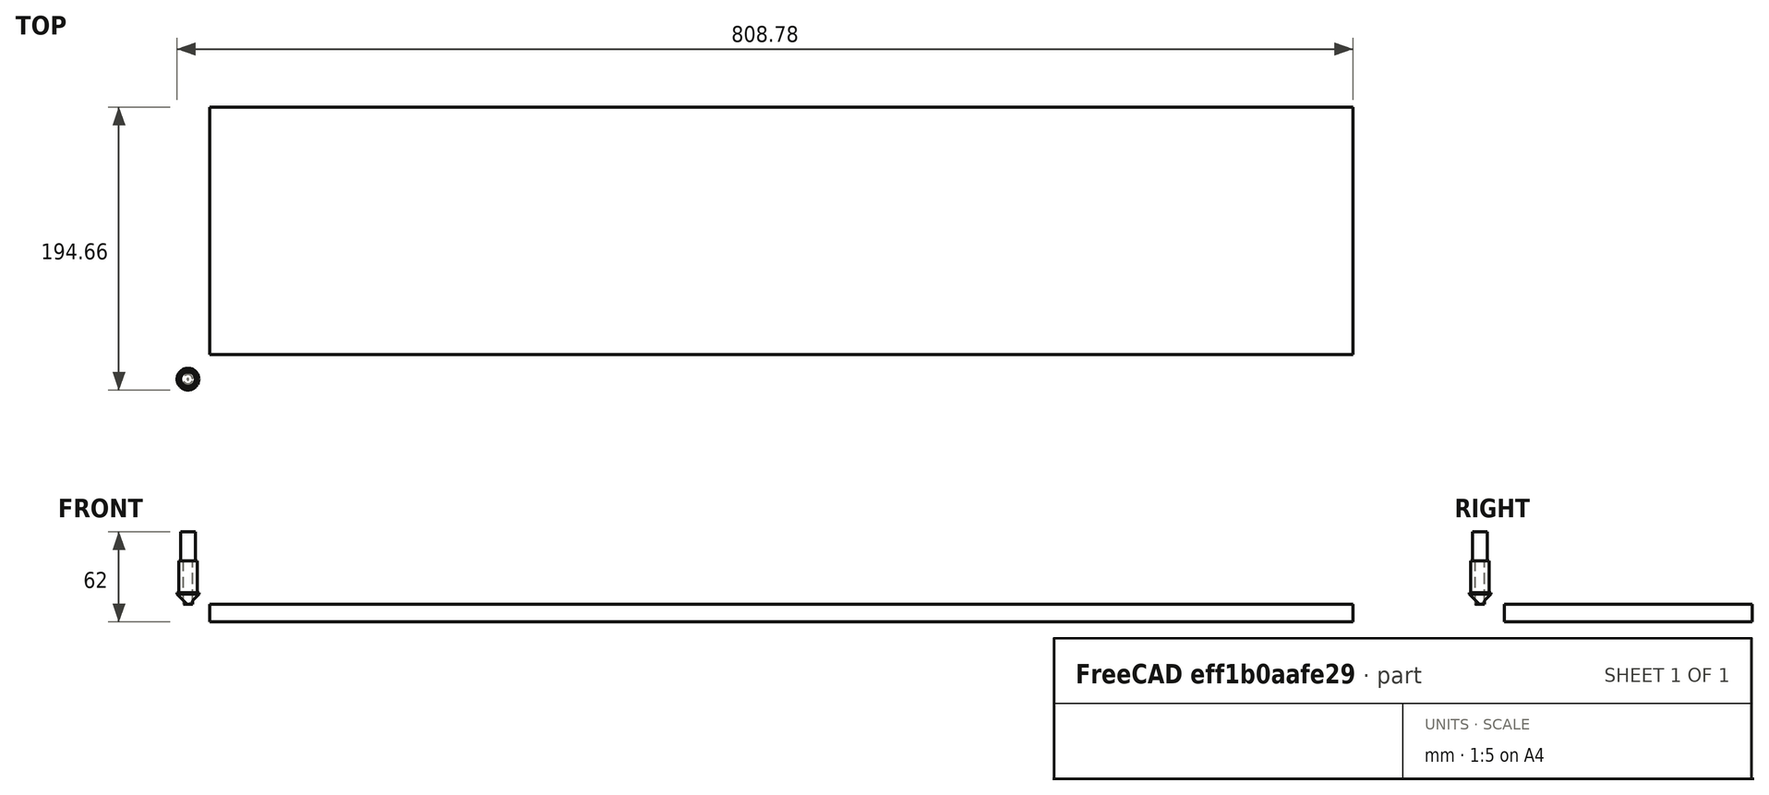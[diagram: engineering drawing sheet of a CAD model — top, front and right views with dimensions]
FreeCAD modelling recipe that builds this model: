
FCSTD DOCUMENT  (FreeCAD 0.19RUnknown)
Label: SignsVCarve
License: All rights reserved
LicenseURL: http://en.wikipedia.org/wiki/All_rights_reserved
objects: Path::FeaturePython×5, Part::FeaturePython×4, Spreadsheet::Sheet×2, Part::Part2DObjectPython×2, App::DocumentObjectGroup×2, Sketcher::SketchObject×1, PartDesign::Pad×1, PartDesign::Fillet×1, PartDesign::Body×1, App::FeaturePython×1, Path::FeatureCompoundPython×1, Mesh::FeaturePython×1
note: 13 computed .brp shape members not serialized (recipe doc carries the construction recipe); baked Part::Feature solids carry a one-line shape summary decoded from their .brp

FEATURE [Sketcher::SketchObject] Sketch
  FullyConstrained = true
  MapMode = 5
  Support = -> [XY_Plane]
  expr: Constraints[11] = <<SignSizes>>.XOffset
  expr: Constraints[10] = <<SignSizes>>.YOffset
  expr: Constraints[9] = <<SignSizes>>.Width
  expr: Constraints[8] = <<SignSizes>>.Length
  sketch-geometry (4):
    g0: LineSegment StartX=8.68 StartY=187.16 StartZ=0 EndX=998.84 EndY=187.16 EndZ=0
    g1: LineSegment StartX=998.84 StartY=187.16 StartZ=0 EndX=998.84 EndY=42.44 EndZ=0
    g2: LineSegment StartX=998.84 StartY=42.44 StartZ=0 EndX=8.68 EndY=42.44 EndZ=0
    g3: LineSegment StartX=8.68 StartY=42.44 StartZ=0 EndX=8.68 EndY=187.16 EndZ=0
  constraints (12):
    c: Coincident(g0,g1)
    c: Coincident(g1,g2)
    c: Coincident(g2,g3)
    c: Coincident(g3,g0)
    c: Horizontal(g0)
    c: Horizontal(g2)
    c: Vertical(g1)
    c: Vertical(g3)
    c: DistanceX(g2,g1) = 990.16
    c: DistanceY(g2,g0) = 144.72
    c: DistanceY(g-1,g2) = 42.44
    c: DistanceX(g-1,g2) = 8.68
FEATURE [Spreadsheet::Sheet] Spreadsheet  label="SignSizes"
  cells = A1=Sign Length; B1(Length)==B9 + 50mm; A2=Sign Width; B2(Width)==B10 + 50mm; A3=Sign Thickness; B3(Thickness)=12; A4=X Offset; B4(XOffset)==B15 - B14; A5=Y Offset; B5(YOffset)==B16 - B14; A7=Text Information Read from Shapestring; A8=String; B8==<<ShapeString>>.String; A9=Text Length; B9==<<ShapeString>>.Shape.BoundBox.XLength * 1mm; A10=Text Width; B10==<<ShapeString>>.Shape.BoundBox.YLength * 1mm; A11=Font Size; B11==<<ShapeString>>.Size; A12=Text X Location; B12==<<ShapeString>>.Placement.Base.x; A13=Text X Location; B13==<<ShapeString>>.Placement.Base.y; A14=Margin; B14==25mm; A15=X Text Location; B15==<<ShapeString>>.Shape.BoundBox.XMin * 1mm; A16=Y Text Location; B16==<<ShapeString>>.Shape.BoundBox.YMin * 1mm
FEATURE [PartDesign::Pad] Pad
  Direction = (1,1,1)
  Length = 12
  Length2 = 100
  Profile = -> Sketch
  Reversed = true
  Type = 0
  expr: Length = <<SignSizes>>.Thickness
FEATURE [Part::Part2DObjectPython] ShapeString  # Draft 2D object (typed FeaturePython)
  FontFile = <path>
  Placement = pos=(30,70,0) rot=(0,0,1;0rad)
  Size = 48
  String = The Men's Shed Router
  Tracking = 0
  expr: Size = <<Text Properties>>.SignFontSize
  expr: String = <<Text Properties>>.SignText
  expr: .Placement.Base.x = 30
  expr: .Placement.Base.y = 70
FEATURE [PartDesign::Fillet] Fillet
  Base = -> Pad [Edge8,Edge5,Edge1,Edge2]
  BaseFeature = -> Pad
  Radius = 20
  Refine = true
  SupportTransform = false
FEATURE [PartDesign::Body] Body  label="Rectangle"
  Group = -> [Sketch,Pad,Fillet]
  Origin = -> Origin
  Tip = -> Fillet
FEATURE [Spreadsheet::Sheet] Spreadsheet001  label="Text Properties"
  cells = A3=Sign Text; B3(SignText)=The Men's Shed Router; A4=Font Size; B4(SignFontSize)=48; A5=Text Groove Depth; B5(textGrooveDepth)=-4
FEATURE [App::FeaturePython] SetupSheet  # Path/CAM operation (typed FeaturePython)
  ClearanceHeightExpression = OpStockZMax+SetupSheet.ClearanceHeightOffset
  ClearanceHeightOffset = 5
  CoolantMode = 0
  CoolantModes = None | Flood | Mist
  FinalDepthExpression = OpFinalDepth
  HorizRapid = 0
  SafeHeightExpression = OpStockZMax+SetupSheet.SafeHeightOffset
  SafeHeightOffset = 3
  StartDepthExpression = OpStartDepth
  StepDownExpression = OpToolDiameter
  VertRapid = 0
FEATURE [Part::FeaturePython] Clone  label="Model-Rectangle"  # Draft clone (typed FeaturePython)
  AttacherType = Attacher::AttachEngine3D
  Fuse = false
  Objects = -> [Body]
  PathResource = Model
  Scale = (1,1,1)
FEATURE [Part::Part2DObjectPython] Clone2D  label="Model-ShapeString"  # Draft 2D object (typed FeaturePython)
  Fuse = false
  Objects = -> [ShapeString]
  PathResource = Model
  Placement = pos=(30,70,0) rot=(0,0,1;0rad)
  Scale = (1,1,1)
FEATURE [App::DocumentObjectGroup] Model
  Group = -> [Clone,Clone2D]
FEATURE [Part::FeaturePython] Stock001  # WARN: FeaturePython — macro-defined, semantics opaque (R4)
  Height = 12
  Length = 786.36
  Placement = pos=(14.92,16.84,-12) rot=(0,0,1;0rad)
  StockType = CreateBox
  Width = 170.32
FEATURE [Part::FeaturePython] ToolBit001  label="6.4mm Endmill"  # Path/CAM toolbit (typed FeaturePython)
  BitPropertyNames = Chipload | CuttingEdgeHeight | Diameter | Flutes | Length | Material | ShankDiameter
  BitShape = /app/freecad/Mod/Path/Tools/Shape/endmill.fcstd
  Chipload = 0
  CuttingEdgeHeight = 30
  Diameter = 6.4
  File = <userpath>/MensShed/CNCRouter/FreeCAD/Bit/6.4mm_Endmill.fctb
  Flutes = 0
  Length = 50
  Material = 0
  ShankDiameter = 10
  ShapeName = endmill
FEATURE [Path::FeaturePython] __4mm_Endmill  label="6.4mm Endmill001"  # Path/CAM operation (typed FeaturePython)
  HorizFeed = 10
  HorizRapid = 0
  SpindleDir = 0
  SpindleSpeed = 10000
  Tool = -> ToolBit001
  ToolNumber = 2
  VertFeed = 10
  VertRapid = 0
  expr: HorizRapid = SetupSheet.HorizRapid
  expr: VertRapid = SetupSheet.VertRapid
FEATURE [Part::FeaturePython] ToolBit002  label="90 Deg. V-Bit"  # Path/CAM toolbit (typed FeaturePython)
  BitPropertyNames = Chipload | CuttingEdgeAngle | CuttingEdgeHeight | Diameter | Flutes | Length | Material | ShankDiameter | TipDiameter
  BitShape = /app/freecad/Mod/Path/Tools/Shape/v-bit.fcstd
  Chipload = 0
  CuttingEdgeAngle = 90
  CuttingEdgeHeight = 1
  Diameter = 15
  File = <userpath>/MensShed/CNCRouter/FreeCAD/Bit/90degree_Vbit.fctb
  Flutes = 0
  Length = 30
  Material = 0
  ShankDiameter = 12.7
  ShapeName = v_bit
  TipDiameter = 1
FEATURE [Path::FeaturePython] _0_Deg__V_Bit  label="90 Deg. V-Bit001"  # Path/CAM operation (typed FeaturePython)
  HorizFeed = 10
  HorizRapid = 0
  SpindleDir = 0
  SpindleSpeed = 10000
  Tool = -> ToolBit002
  ToolNumber = 3
  VertFeed = 10
  VertRapid = 0
  expr: HorizRapid = SetupSheet.HorizRapid
  expr: VertRapid = SetupSheet.VertRapid
FEATURE [App::DocumentObjectGroup] Tools
  Group = -> [__4mm_Endmill,_0_Deg__V_Bit]
FEATURE [Path::FeaturePython] Profile  # Path/CAM operation (typed FeaturePython)
  Active = true
  AreaParams:
    Tolerance = 1e-07
    FitArcs = True
    Simplify = False
    CleanDistance = 0.0
    Accuracy = 0.01
    Unit = 1.0
    MinArcPoints = 4
    MaxArcPoints = 100
    ClipperScale = 10000000.0
    Fill = 0
    Coplanar = 0
    Reorient = True
    Outline = False
    Explode = False
    OpenMode = 0
    Deflection = 0.01
    SubjectFill = 0
    ClipFill = 0
    Offset = 3.2
    ExtraPass = 0
    Stepover = 0.0
    LastStepover = 0.0
    JoinType = 0
    EndType = 0
    MiterLimit = 2.0
    RoundPrecision = 0.0
    PocketMode = 0
    ToolRadius = 1.0
    PocketExtraOffset = 0.0
    PocketStepover = 0.0
    PocketLastStepover = 0.0
    FromCenter = False
    Angle = 45.0
    AngleShift = 0.0
    Shift = 0.0
    Thicken = False
    SectionCount = -1
    Stepdown = 1.0
    SectionOffset = 0.0
    SectionTolerance = 1e-06
    SectionMode = 2
    Project = False
  AttemptInverseAngle = true
  Base = -> [Clone]
  ClearanceHeight = 5
  CoolantMode = None
  CycleTime = 00:05:23
  Direction = 0
  EnableRotation = 0
  FinalDepth = 12
  HandleMultipleFeatures = 0
  InverseAngle = false
  JoinType = 0
  LimitDepthToFace = true
  MiterLimit = 0.1
  OffsetExtra = 0
  OpFinalDepth = -12
  OpStartDepth = 0
  OpStockZMax = 0
  OpStockZMin = -12
  OpToolDiameter = 6.4
  PathParams = {'orientation': 1, 'feedrate': 10.0, 'feedrate_v': 10.0, 'verbose': True, 'resume_height': 3.0, 'retraction': 5.0, 'return_end': True, 'preamble': False}
  ReverseDirection = false
  SafeHeight = 3
  Side = 0
  StartDepth = 0
  StartPoint = (0,0,0)
  StepDown = 6.4
  ToolController = -> __4mm_Endmill
  UseComp = true
  UseStartPoint = false
  processCircles = false
  processHoles = false
  processPerimeter = true
  expr: ClearanceHeight = OpStockZMax + SetupSheet.ClearanceHeightOffset
  expr: SafeHeight = OpStockZMax + SetupSheet.SafeHeightOffset
  expr: StepDown = OpToolDiameter
  expr: FinalDepth = <<SignSizes>>.Thickness
  expr: StartDepth = OpStartDepth
FEATURE [Path::FeaturePython] Vcarve  # Path/CAM operation (typed FeaturePython)
  Active = true
  ClearanceHeight = 5
  Colinear = 10
  CoolantMode = None
  CycleTime = 00:00:00
  Discretize = 0.01
  FinalDepth = -4
  OpFinalDepth = -12
  OpStartDepth = 0
  OpStockZMax = 0
  OpStockZMin = -12
  OpToolDiameter = 15
  SafeHeight = 3
  StartDepth = 0
  Tolerance = 0.01
  ToolController = -> _0_Deg__V_Bit
  expr: ClearanceHeight = OpStockZMax + SetupSheet.ClearanceHeightOffset
  expr: SafeHeight = OpStockZMax + SetupSheet.SafeHeightOffset
  expr: FinalDepth = <<Text Properties>>.textGrooveDepth
  expr: StartDepth = OpStartDepth
FEATURE [Path::FeatureCompoundPython] Operations  # Path/CAM operation (typed FeaturePython)
  Group = -> [Profile,Vcarve]
  UsePlacements = false
FEATURE [Path::FeaturePython] Job  # Path/CAM operation (typed FeaturePython)
  CycleTime = 00:05:23
  Fixtures = G54
  GeometryTolerance = 0.01
  LastPostProcessDate = 2022-01-29 14:08:16.850529
  LastPostProcessOutput = <userpath>/MensShed/CNCRouter/Signs/SignsVCarve.ngc
  Model = -> Model
  Operations = -> Operations
  OrderOutputBy = 0
  PostProcessor = 7
  PostProcessorOutputFile = %D/%d.ngc
  SetupSheet = -> SetupSheet
  SplitOutput = false
  Stock = -> Stock001
  Tools = -> Tools
FEATURE [Mesh::FeaturePython] CutMaterial  # WARN: FeaturePython — macro-defined, semantics opaque (R4)
note: 1 file-system path scrubbed to <path> (originals preserved in the JSON sidecar)
